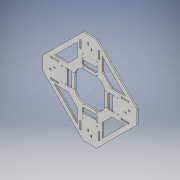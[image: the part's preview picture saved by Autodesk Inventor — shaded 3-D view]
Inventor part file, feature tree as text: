
AUTODESK INVENTOR PART (.ipt)
format: ipt  version: 2017 (Build 210142000, 142)  size: 365,056 bytes
history: native  units: in
note: dims shown in document units (in); Inventor stores cm internally (conversion verified against a paired STEP export)
features: reference x29, other x8, plane x2, extrude x1, chamfer x1, sketch x1
ambient origin geometry x8: Origin, YZ Plane, XZ Plane, XY Plane, X Axis, Y Axis, Z Axis, Center Point
bodies: Solid1 (feature_tree)
feature tree (42):
  extrude  "Extrusion1"  Depth=4.75in
  chamfer  "Chamfer1"  Distance=0.2087in
  other  "Work Axis1"
  sketch  "Sketch1"  dims[d0=4.75in d1=4.75in d7=0.2087in d8=0.0in d11=12.0in d12=12.0in d13=1.5748in d14=0.5906in d15=1.5748in d17=360.0deg d19=1.5in d20=0.125in d21=45.0deg d22=0.75in d24=1.25in d25=0.2087in d26=1.5748in d28=360.0deg d30=1.5748in d32=360.0deg d34=1.5748in d36=360.0deg]
  plane  "Work Plane1"
  plane  "Work Plane2"
  reference  "Reference4"
  reference  "Reference5"
  reference  "Reference6"
  reference  "Reference7"
  reference  "Reference9"
  reference  "Reference10"
  reference  "Reference11"
  reference  "Reference12"
  reference  "Reference13"
  reference  "Reference14"
  reference  "Reference15"
  reference  "Reference16"
  reference  "Reference17"
  reference  "Reference18"
  reference  "Reference19"
  reference  "Reference20"
  reference  "Reference21"
  reference  "Reference22"
  reference  "Reference23"
  reference  "Reference24"
  reference  "Reference25"
  reference  "Reference26"
  reference  "Reference27"
  reference  "Reference28"
  reference  "Reference29"
  reference  "Reference30"
  reference  "Reference31"
  reference  "Reference32"
  reference  "Reference33"
  other  "Rubiks Cube Solver.iam"
  other  "stepper mount:1"
  other  "bearing block:2"
  other  "riser:1"
  other  "bearing block:1"
  other  "leg:1"
  other  "leg:2"
